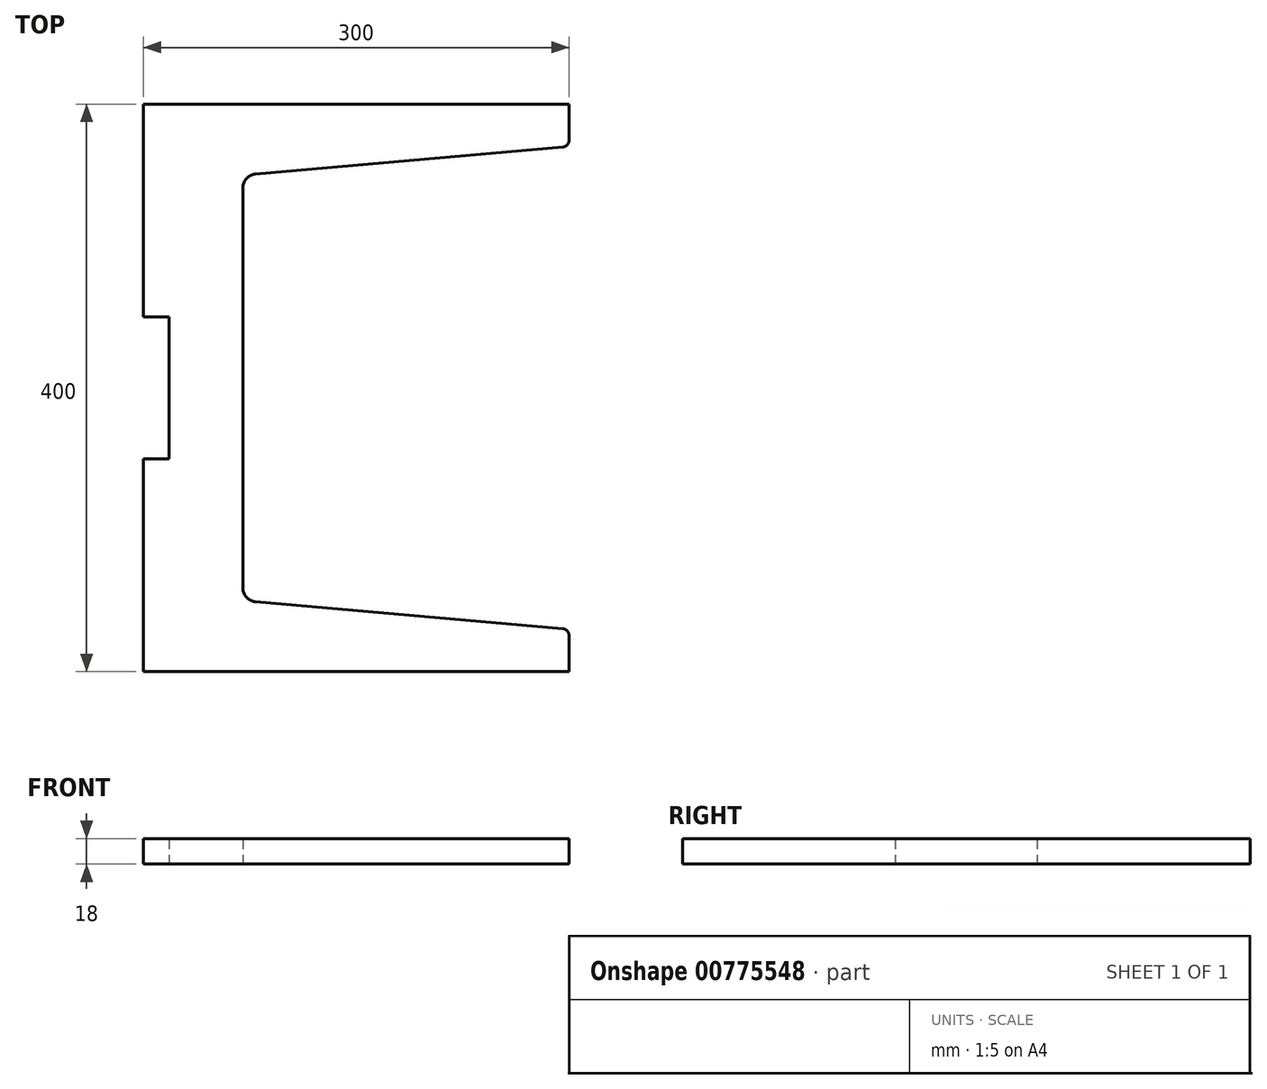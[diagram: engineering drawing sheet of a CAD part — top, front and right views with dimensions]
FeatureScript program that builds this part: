
annotation { "Feature Type Name" : "Feature", "Feature Type Description" : "" }
export const myFeature = defineFeature(function(context is Context, id is Id, definition is map)
    precondition{}
    {
        {
            var Q0;
            Q0=qCreatedBy(makeId("Top.planeOp"),FACE);
            var sketch = newSketch(context, id + "F0", { "sketchPlane" : qUnion([Q0])});
            skLineSegment(sketch, "E0", {"start": v(0, 400) * mm, "end": v(300, 400) * mm});
            skLineSegment(sketch, "E1", {"start": v(300, 400) * mm, "end": v(300, 374.58) * mm});
            skLineSegment(sketch, "E2", {"start": v(295.44, 369.6) * mm, "end": v(79.13, 350.68) * mm});
            skLineSegment(sketch, "E3", {"start": v(300, 25.42) * mm, "end": v(300, 0) * mm});
            skLineSegment(sketch, "E4", {"start": v(300, 0) * mm, "end": v(0, 0) * mm});
            skLineSegment(sketch, "E5", {"start": v(0, 400) * mm, "end": v(0, 250) * mm});
            skLineSegment(sketch, "E6", {"start": v(79.13, 49.32) * mm, "end": v(295.44, 30.4) * mm});
            skLineSegment(sketch, "E7", {"start": v(70, 340.71) * mm, "end": v(70, 59.29) * mm});
            skPoint(sketch, "E8.visualSharp", {"position": v(300, 370) * mm});
            skArc(sketch, "E8.filletArc", {"start": v(295.44, 369.6) * mm, "mid": v(298.69, 371.2) * mm, "end": v(300, 374.58) * mm});
            skPoint(sketch, "E9.visualSharp", {"position": v(300, 30) * mm});
            skArc(sketch, "E9.filletArc", {"start": v(300, 25.42) * mm, "mid": v(298.69, 28.8) * mm, "end": v(295.44, 30.4) * mm});
            skPoint(sketch, "E10.visualSharp", {"position": v(70, 349.88) * mm});
            skArc(sketch, "E10.filletArc", {"start": v(79.13, 350.68) * mm, "mid": v(72.63, 347.47) * mm, "end": v(70, 340.71) * mm});
            skPoint(sketch, "E11.visualSharp", {"position": v(70, 50.12) * mm});
            skArc(sketch, "E11.filletArc", {"start": v(70, 59.29) * mm, "mid": v(72.63, 52.53) * mm, "end": v(79.13, 49.32) * mm});
            skLineSegment(sketch, "E12", {"start": v(0, 250) * mm, "end": v(0, 250) * mm});
            skLineSegment(sketch, "E13", {"start": v(18, 250) * mm, "end": v(18, 150) * mm});
            skLineSegment(sketch, "E14", {"start": v(18, 150) * mm, "end": v(0, 150) * mm});
            skLineSegment(sketch, "E15", {"start": v(0, 250) * mm, "end": v(18, 250) * mm});
            skLineSegment(sketch, "E16", {"start": v(0, 150) * mm, "end": v(0, 150) * mm});
            skLineSegment(sketch, "E17", {"start": v(0, 150) * mm, "end": v(0, 0) * mm});
            skLineSegment(sketch, "E18", {"start": v(0, 297.27) * mm, "end": v(0, 250) * mm});
            skSolve(sketch);
        }
        {
            var Q0;
            Q0=makeQuery(id+"F0.imprint","IMPRINT",FACE,{"disambiguationData":[TD([[makeQuery(id+"F0.imprint","IMPRINT",EDGE,{"derivedFrom":sQuery(id+"F0.wireOp",EDGE,"E0")}),-1.0]])]});
            extrude(context, id + "F1", {"entities" : qUnion([Q0]), "depth" : 18 * mm, "offsetDistance" : 25 * mm});
        }
        {
            var Q0;
            Q0=makeQuery(id+"F1.opExtrude","SWEPT_FACE",FACE,{"disambiguationData":[OSD([sQuery(id+"F0.wireOp",EDGE,"E0")])]});
            var sketch = newSketch(context, id + "F2", { "sketchPlane" : qUnion([Q0])});
            skLineSegment(sketch, "E19", {"start": v(0, 9) * mm, "end": v(-50, 9) * mm, "construction": true});
            skSolve(sketch);
        }
        {
            var Q0;
            Q0=makeQuery(id+"F1.opExtrude","SWEPT_FACE",FACE,{"disambiguationData":[OSD([sQuery(id+"F0.wireOp",EDGE,"E4")])]});
            var sketch = newSketch(context, id + "F3", { "sketchPlane" : qUnion([Q0])});
            skLineSegment(sketch, "E20", {"start": v(0, 9) * mm, "end": v(50, 9) * mm, "construction": true});
            skSolve(sketch);
        }
        {
            var Q0;
            Q0=makeQuery(id+"F1.opExtrude","SWEPT_FACE",FACE,{"disambiguationData":[OSD([sQuery(id+"F0.wireOp",EDGE,"E13")])]});
            var sketch = newSketch(context, id + "F4", { "sketchPlane" : qUnion([Q0])});
            skLineSegment(sketch, "E21", {"start": v(-250, 9) * mm, "end": v(-200, 9) * mm, "construction": true});
            skSolve(sketch);
        }
    });
